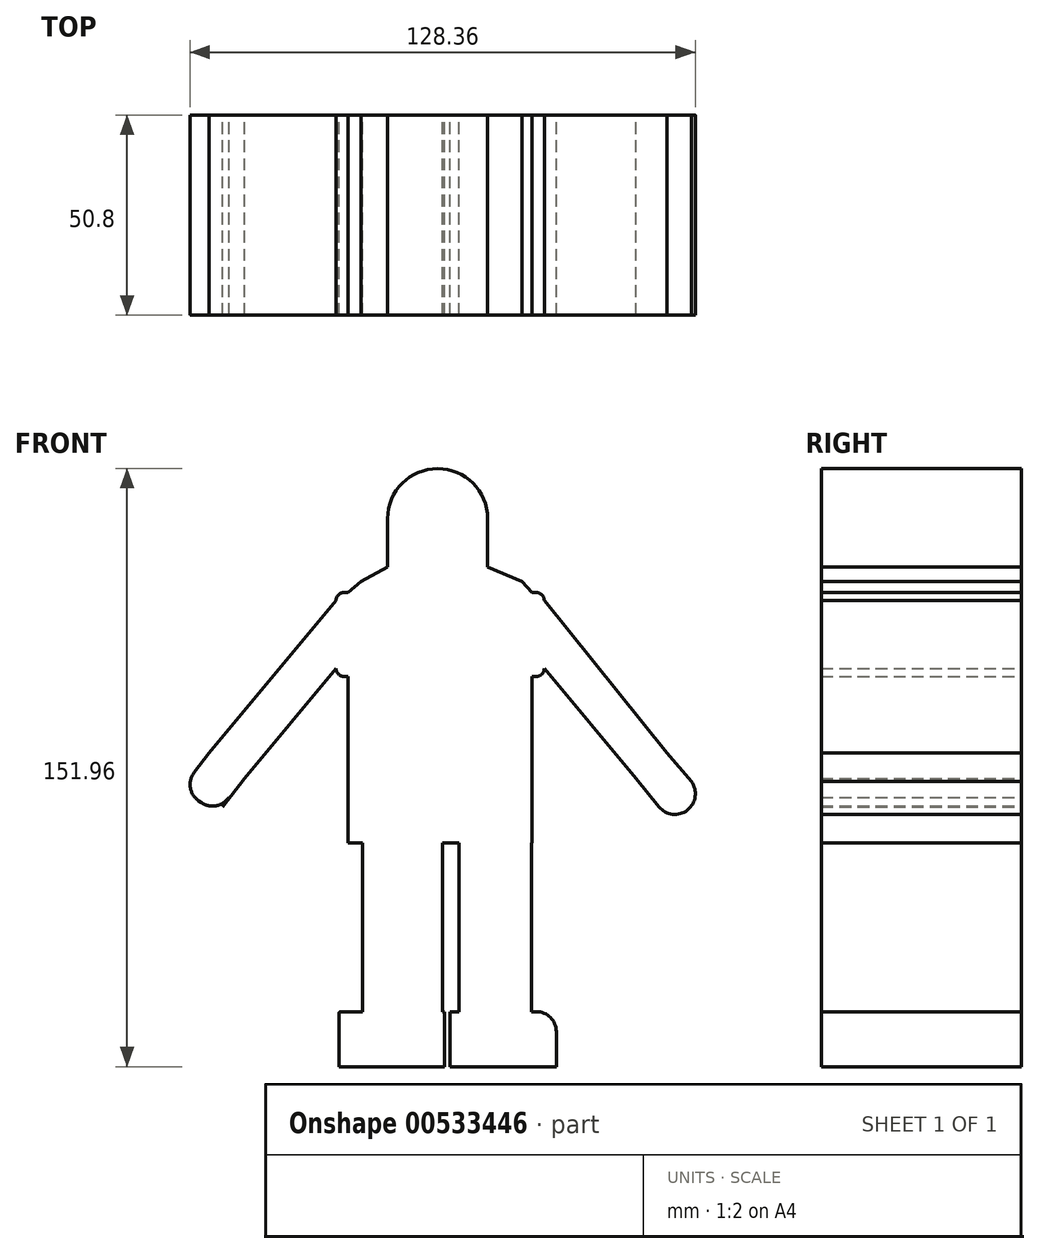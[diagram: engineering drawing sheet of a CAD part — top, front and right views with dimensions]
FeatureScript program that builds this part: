
annotation { "Feature Type Name" : "Feature", "Feature Type Description" : "" }
export const myFeature = defineFeature(function(context is Context, id is Id, definition is map)
    precondition{}
    {
        {
            var Q0;
            Q0=qCreatedBy(makeId("Front.planeOp"),FACE);
            var sketch = newSketch(context, id + "F0", { "sketchPlane" : qUnion([Q0])});
            skLineSegment(sketch, "E0", {"start": v(11, 53.66) * mm, "end": v(11, 55.12) * mm});
            skLineSegment(sketch, "E1", {"start": v(11, 55.12) * mm, "end": v(11, 58.6) * mm});
            skLineSegment(sketch, "E2", {"start": v(11, 58.6) * mm, "end": v(11, 62.32) * mm});
            skLineSegment(sketch, "E3", {"start": v(-14.4, 53.66) * mm, "end": v(-14.4, 55.12) * mm});
            skLineSegment(sketch, "E4", {"start": v(-14.4, 55.12) * mm, "end": v(-14.4, 58.6) * mm});
            skLineSegment(sketch, "E5", {"start": v(-14.4, 58.6) * mm, "end": v(-14.4, 62.32) * mm});
            skLineSegment(sketch, "E6", {"start": v(-14.4, 62.32) * mm, "end": v(-14.4, 66) * mm});
            skLineSegment(sketch, "E7", {"start": v(-1.7, 78.7) * mm, "end": v(-1.7, 78.7) * mm});
            skLineSegment(sketch, "E8", {"start": v(11, 66) * mm, "end": v(11, 62.32) * mm});
            skPoint(sketch, "E9.visualSharp", {"position": v(-14.4, 78.7) * mm});
            skArc(sketch, "E9.filletArc", {"start": v(-1.7, 78.7) * mm, "mid": v(-10.69, 74.98) * mm, "end": v(-14.4, 66) * mm});
            skPoint(sketch, "E10.visualSharp", {"position": v(11, 78.7) * mm});
            skArc(sketch, "E10.filletArc", {"start": v(11, 66) * mm, "mid": v(7.27, 74.98) * mm, "end": v(-1.7, 78.7) * mm});
            skLineSegment(sketch, "E11", {"start": v(-9.33, 48.58) * mm, "end": v(-1.7, 48.58) * mm});
            skLineSegment(sketch, "E12", {"start": v(-1.7, 48.58) * mm, "end": v(5.91, 48.58) * mm});
            skPoint(sketch, "E13.visualSharp", {"position": v(-14.4, 48.58) * mm});
            skArc(sketch, "E13.filletArc", {"start": v(-14.4, 53.66) * mm, "mid": v(-12.92, 50.07) * mm, "end": v(-9.33, 48.58) * mm});
            skPoint(sketch, "E14.visualSharp", {"position": v(11, 48.58) * mm});
            skArc(sketch, "E14.filletArc", {"start": v(5.91, 48.58) * mm, "mid": v(9.5, 50.07) * mm, "end": v(11, 53.66) * mm});
            skLineSegment(sketch, "E15", {"start": v(-14.4, 53.66) * mm, "end": v(-21.16, 50.07) * mm});
            skPoint(sketch, "E15.endSnap0", {"position": v(-12.92, 50.07) * mm});
            skLineSegment(sketch, "E16", {"start": v(-21.16, 50.07) * mm, "end": v(-24.45, 47.2) * mm});
            skLineSegment(sketch, "E17", {"start": v(-24.45, 47.2) * mm, "end": v(-24.45, -16.42) * mm});
            skLineSegment(sketch, "E18", {"start": v(11, 53.66) * mm, "end": v(19.76, 50.07) * mm});
            skLineSegment(sketch, "E19", {"start": v(19.76, 50.07) * mm, "end": v(22.26, 47.2) * mm});
            skLineSegment(sketch, "E20", {"start": v(22.26, 47.2) * mm, "end": v(22.26, -16.42) * mm});
            skLineSegment(sketch, "E21", {"start": v(22.26, -16.42) * mm, "end": v(-24.45, -16.42) * mm});
            skLineSegment(sketch, "E22", {"start": v(-20.75, -16.42) * mm, "end": v(-20.75, -59.28) * mm});
            skLineSegment(sketch, "E23", {"start": v(-20.75, -59.28) * mm, "end": v(-0.43, -59.28) * mm});
            skLineSegment(sketch, "E24", {"start": v(-0.43, -59.28) * mm, "end": v(-0.43, -16.42) * mm});
            skLineSegment(sketch, "E25", {"start": v(3.67, -16.42) * mm, "end": v(3.67, -59.28) * mm});
            skLineSegment(sketch, "E26", {"start": v(3.67, -59.28) * mm, "end": v(22.18, -59.28) * mm});
            skLineSegment(sketch, "E27", {"start": v(22.18, -59.28) * mm, "end": v(22.18, -16.42) * mm});
            skLineSegment(sketch, "E28.bottom", {"start": v(22.26, 47.2) * mm, "end": v(23.33, 47.2) * mm});
            skLineSegment(sketch, "E28.top", {"start": v(22.26, 25.85) * mm, "end": v(23.33, 25.85) * mm});
            skLineSegment(sketch, "E28.left", {"start": v(22.26, 47.2) * mm, "end": v(22.26, 25.85) * mm});
            skLineSegment(sketch, "E28.right", {"start": v(25.37, 45.17) * mm, "end": v(25.37, 27.89) * mm});
            skPoint(sketch, "E29.visualSharp", {"position": v(25.37, 25.85) * mm});
            skArc(sketch, "E29.filletArc", {"start": v(23.33, 25.85) * mm, "mid": v(24.77, 26.45) * mm, "end": v(25.37, 27.89) * mm});
            skPoint(sketch, "E30.visualSharp", {"position": v(25.37, 47.2) * mm});
            skArc(sketch, "E30.filletArc", {"start": v(25.37, 45.17) * mm, "mid": v(24.77, 46.6) * mm, "end": v(23.33, 47.2) * mm});
            skLineSegment(sketch, "E31.bottom", {"start": v(-24.45, 47.2) * mm, "end": v(-25.52, 47.2) * mm});
            skLineSegment(sketch, "E31.top", {"start": v(-24.45, 25.85) * mm, "end": v(-25.52, 25.85) * mm});
            skLineSegment(sketch, "E31.left", {"start": v(-24.45, 47.2) * mm, "end": v(-24.45, 25.85) * mm});
            skLineSegment(sketch, "E31.right", {"start": v(-27.55, 45.17) * mm, "end": v(-27.55, 27.89) * mm});
            skPoint(sketch, "E32.visualSharp", {"position": v(-27.55, 47.2) * mm});
            skArc(sketch, "E32.filletArc", {"start": v(-25.52, 47.2) * mm, "mid": v(-26.95, 46.6) * mm, "end": v(-27.55, 45.17) * mm});
            skPoint(sketch, "E33.visualSharp", {"position": v(-27.55, 25.85) * mm});
            skArc(sketch, "E33.filletArc", {"start": v(-27.55, 27.89) * mm, "mid": v(-26.95, 26.45) * mm, "end": v(-25.52, 25.85) * mm});
            skLineSegment(sketch, "E34", {"start": v(25.37, 45.17) * mm, "end": v(56.57, 6.5) * mm});
            skLineSegment(sketch, "E35", {"start": v(56.57, 6.5) * mm, "end": v(52.17, 2.95) * mm});
            skLineSegment(sketch, "E36", {"start": v(52.17, 2.95) * mm, "end": v(48.65, 0) * mm});
            skLineSegment(sketch, "E37", {"start": v(48.65, 0) * mm, "end": v(25.37, 27.89) * mm});
            skPoint(sketch, "E38.endSnap0", {"position": v(22.26, 15.4) * mm});
            skLineSegment(sketch, "E39", {"start": v(-27.55, 27.89) * mm, "end": v(-50.84, 0) * mm});
            skLineSegment(sketch, "E40", {"start": v(-27.55, 45.17) * mm, "end": v(-59.84, 6.5) * mm});
            skLineSegment(sketch, "E41", {"start": v(-59.84, 6.5) * mm, "end": v(-50.84, 0) * mm});
            skLineSegment(sketch, "E42", {"start": v(48.65, 0) * mm, "end": v(54.48, -7.22) * mm});
            skArc(sketch, "E43", {"start": v(54.48, -7.22) * mm, "mid": v(61.75, -8.06) * mm, "end": v(62.71, -0.8) * mm});
            skLineSegment(sketch, "E44", {"start": v(62.71, -0.8) * mm, "end": v(56.57, 6.5) * mm});
            skLineSegment(sketch, "E45", {"start": v(65.66, 0.88) * mm, "end": v(65.66, 0.86) * mm});
            skLineSegment(sketch, "E46", {"start": v(-56.4, -7.22) * mm, "end": v(-50.84, 0) * mm});
            skLineSegment(sketch, "E47", {"start": v(-54.77, -4.86) * mm, "end": v(-56.4, -7.22) * mm});
            skLineSegment(sketch, "E48", {"start": v(-61.84, -6.15) * mm, "end": v(-62.42, -5.74) * mm});
            skLineSegment(sketch, "E49", {"start": v(-63.6, 1.47) * mm, "end": v(-59.84, 6.5) * mm});
            skPoint(sketch, "E50.visualSharp", {"position": v(-66.74, -2.75) * mm});
            skArc(sketch, "E50.filletArc", {"start": v(-63.6, 1.47) * mm, "mid": v(-64.54, -2.39) * mm, "end": v(-62.42, -5.74) * mm});
            skPoint(sketch, "E51.visualSharp", {"position": v(-57.66, -9.04) * mm});
            skArc(sketch, "E51.filletArc", {"start": v(-61.84, -6.15) * mm, "mid": v(-58.04, -6.97) * mm, "end": v(-54.77, -4.86) * mm});
            skLineSegment(sketch, "E52", {"start": v(0, -59.28) * mm, "end": v(0, -73.26) * mm});
            skLineSegment(sketch, "E53", {"start": v(0, -73.26) * mm, "end": v(-26.8, -73.26) * mm});
            skLineSegment(sketch, "E54", {"start": v(-26.8, -73.26) * mm, "end": v(-26.8, -59.79) * mm});
            skLineSegment(sketch, "E55", {"start": v(-26.3, -59.28) * mm, "end": v(-20.75, -59.28) * mm});
            skLineSegment(sketch, "E56", {"start": v(1.39, -59.28) * mm, "end": v(3.67, -59.28) * mm});
            skLineSegment(sketch, "E57", {"start": v(1.39, -59.28) * mm, "end": v(1.39, -73.26) * mm});
            skLineSegment(sketch, "E58", {"start": v(1.39, -73.26) * mm, "end": v(28.42, -73.26) * mm});
            skLineSegment(sketch, "E59", {"start": v(28.42, -73.26) * mm, "end": v(28.42, -64.36) * mm});
            skLineSegment(sketch, "E60", {"start": v(23.34, -59.28) * mm, "end": v(22.18, -59.28) * mm});
            skPoint(sketch, "E61.visualSharp", {"position": v(28.42, -59.28) * mm});
            skArc(sketch, "E61.filletArc", {"start": v(28.42, -64.36) * mm, "mid": v(26.93, -60.77) * mm, "end": v(23.34, -59.28) * mm});
            skLineSegment(sketch, "E62", {"start": v(0, -59.76) * mm, "end": v(0, -59.28) * mm});
            skLineSegment(sketch, "E63", {"start": v(0, -59.28) * mm, "end": v(-0.43, -59.28) * mm});
            skPoint(sketch, "E64.visualSharp", {"position": v(-26.8, -59.28) * mm});
            skArc(sketch, "E64.filletArc", {"start": v(-26.3, -59.28) * mm, "mid": v(-26.66, -59.43) * mm, "end": v(-26.8, -59.79) * mm});
            skSolve(sketch);
        }
        {
            var Q0;
            Q0=makeQuery(id+"F0.imprint","IMPRINT",FACE,{"disambiguationData":[TD([[makeQuery(id+"F0.imprint","IMPRINT",EDGE,{"derivedFrom":sQuery(id+"F0.wireOp",EDGE,"E11")}),-1.0]])]});
            var Q1;
            Q1=makeQuery(id+"F0.imprint","IMPRINT",FACE,{"disambiguationData":[TD([[makeQuery(id+"F0.imprint","IMPRINT",EDGE,{"derivedFrom":sQuery(id+"F0.wireOp",EDGE,"E28.bottom")}),-1.0]])]});
            var Q2;
            Q2=makeQuery(id+"F0.imprint","IMPRINT",FACE,{"disambiguationData":[TD([[makeQuery(id+"F0.imprint","IMPRINT",EDGE,{"derivedFrom":sQuery(id+"F0.wireOp",EDGE,"E28.right")}),1.0]])]});
            var Q3;
            Q3=makeQuery(id+"F0.imprint","IMPRINT",FACE,{"disambiguationData":[TD([[makeQuery(id+"F0.imprint","IMPRINT",EDGE,{"derivedFrom":sQuery(id+"F0.wireOp",EDGE,"E35")}),1.0]])]});
            var Q4;
            Q4=makeQuery(id+"F0.imprint","IMPRINT",FACE,{"disambiguationData":[TD([[makeQuery(id+"F0.imprint","IMPRINT",EDGE,{"derivedFrom":sQuery(id+"F0.wireOp",EDGE,"E31.bottom")}),1.0]])]});
            var Q5;
            Q5=makeQuery(id+"F0.imprint","IMPRINT",FACE,{"disambiguationData":[TD([[makeQuery(id+"F0.imprint","IMPRINT",EDGE,{"derivedFrom":sQuery(id+"F0.wireOp",EDGE,"E31.right")}),-1.0]])]});
            var Q6;
            Q6=makeQuery(id+"F0.imprint","IMPRINT",FACE,{"disambiguationData":[TD([[makeQuery(id+"F0.imprint","IMPRINT",EDGE,{"derivedFrom":sQuery(id+"F0.wireOp",EDGE,"E41")}),-1.0]])]});
            var Q7;
            {var subQ0=sQuery(id+"F0.wireOp",EDGE,"E22");Q7=makeQuery(id+"F0.imprint","IMPRINT",FACE,{"disambiguationData":[TD([[makeQuery(id+"F0.imprint","IMPRINT",EDGE,{"derivedFrom":subQ0}),1.0]])]});}
            var Q8;
            {var subQ0=sQuery(id+"F0.wireOp",EDGE,"E25");Q8=makeQuery(id+"F0.imprint","IMPRINT",FACE,{"disambiguationData":[TD([[makeQuery(id+"F0.imprint","IMPRINT",EDGE,{"derivedFrom":subQ0}),1.0]])]});}
            var Q9;
            Q9=makeQuery(id+"F0.imprint","IMPRINT",FACE,{"disambiguationData":[TD([[makeQuery(id+"F0.imprint","IMPRINT",EDGE,{"derivedFrom":sQuery(id+"F0.wireOp",EDGE,"E26")}),-1.0]])]});
            var Q10;
            Q10=makeQuery(id+"F0.imprint","IMPRINT",FACE,{"disambiguationData":[TD([[makeQuery(id+"F0.imprint","IMPRINT",EDGE,{"derivedFrom":sQuery(id+"F0.wireOp",EDGE,"E23")}),-1.0]])]});
            var Q11;
            Q11=makeQuery(id+"F0.imprint","IMPRINT",FACE,{"disambiguationData":[TD([[makeQuery(id+"F0.imprint","IMPRINT",EDGE,{"derivedFrom":sQuery(id+"F0.wireOp",EDGE,"E0")}),1.0]])]});
            extrude(context, id + "F1", {"entities" : qUnion([Q0, Q1, Q2, Q3, Q4, Q5, Q6, Q7, Q8, Q9, Q10, Q11]), "depth" : 50.8 * mm, "offsetDistance" : 25.4 * mm});
        }
    });
